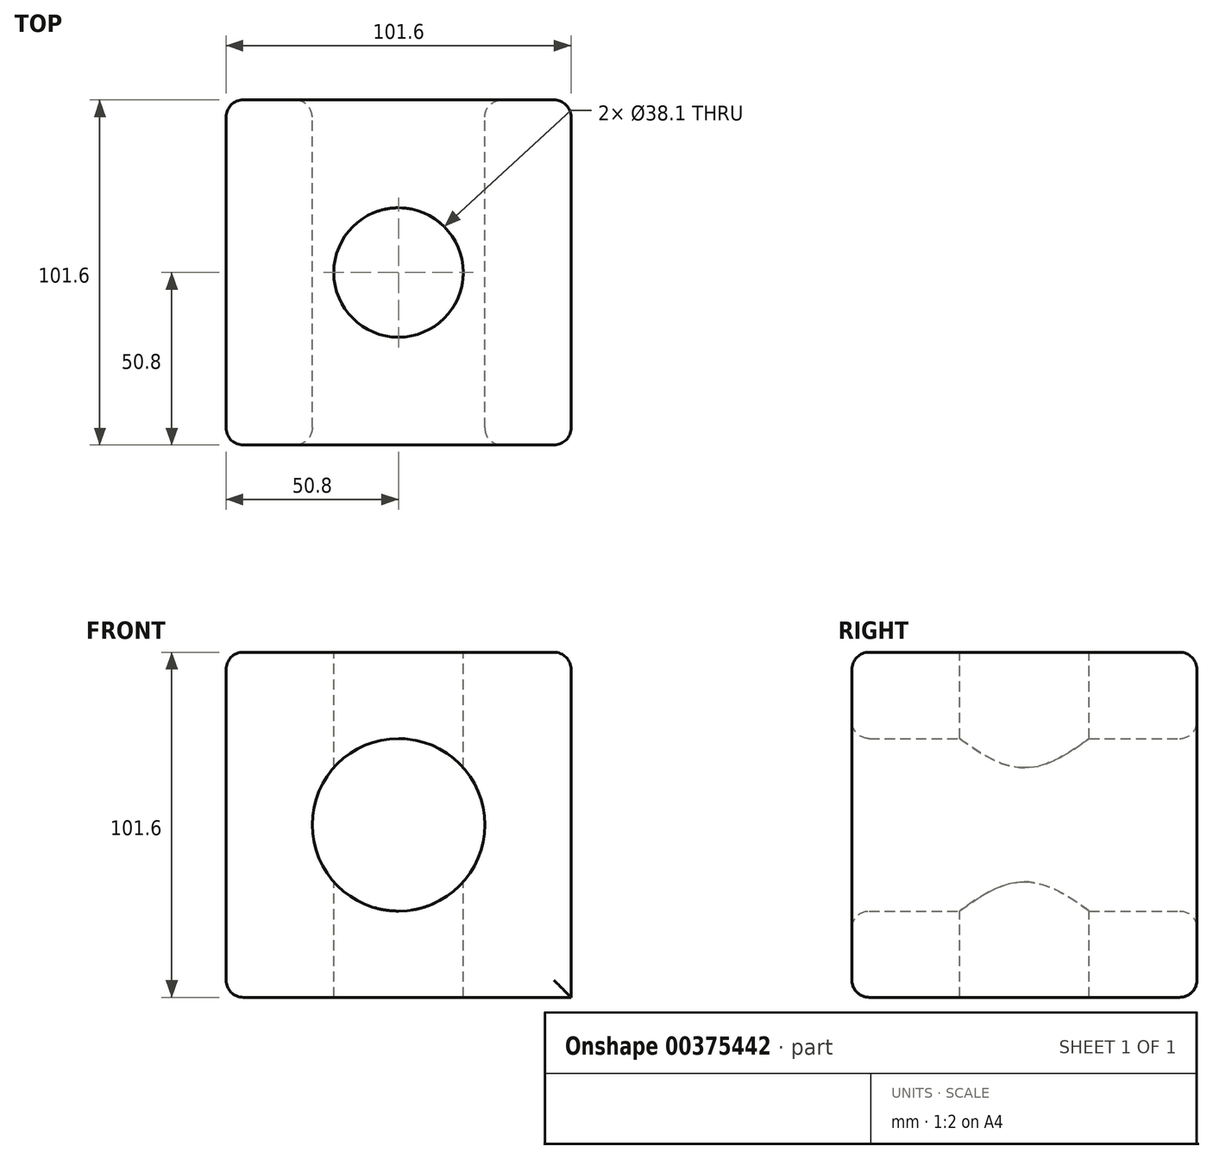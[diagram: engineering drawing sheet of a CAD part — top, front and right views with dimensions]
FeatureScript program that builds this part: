
annotation { "Feature Type Name" : "Feature", "Feature Type Description" : "" }
export const myFeature = defineFeature(function(context is Context, id is Id, definition is map)
    precondition{}
    {
        {
            var Q0;
            Q0=qCreatedBy(makeId("Front.planeOp"),FACE);
            var sketch = newSketch(context, id + "F0", { "sketchPlane" : qUnion([Q0])});
            skLineSegment(sketch, "E0.bottom", {"start": v(-50.8, 50.8) * mm, "end": v(50.8, 50.8) * mm});
            skLineSegment(sketch, "E0.top", {"start": v(-50.8, -50.8) * mm, "end": v(50.8, -50.8) * mm});
            skLineSegment(sketch, "E0.left", {"start": v(-50.8, 50.8) * mm, "end": v(-50.8, -50.8) * mm});
            skLineSegment(sketch, "E0.right", {"start": v(50.8, 50.8) * mm, "end": v(50.8, -50.8) * mm});
            skCircle(sketch, "E1", {"center": v(0, 0) * mm, "radius": 25.4 * mm});
            skSolve(sketch);
        }
        {
            var Q0;
            Q0=makeQuery(id+"F0.imprint","IMPRINT",FACE,{"disambiguationData":[TD([[makeQuery(id+"F0.imprint","IMPRINT",EDGE,{"derivedFrom":sQuery(id+"F0.wireOp",EDGE,"E0.bottom")}),-1.0]])]});
            extrude(context, id + "F1", {"entities" : qUnion([Q0]), "endBound" : BoundingType.SYMMETRIC, "depth" : 101.6 * mm});
        }
        {
            var Q0;
            Q0=makeQuery(id+"F1.opExtrude","CAP_EDGE",EDGE,{"disambiguationData":[OSD([sQuery(id+"F0.wireOp",EDGE,"E0.bottom")])],"isStart":false});
            var Q1;
            Q1=makeQuery(id+"F1.opExtrude","SWEPT_EDGE",EDGE,{"disambiguationData":[OSD([sQuery(id+"F0.wireOp",EDGE,"E0.bottom"),sQuery(id+"F0.wireOp",EDGE,"E0.left")])]});
            var Q2;
            Q2=makeQuery(id+"F1.opExtrude","SWEPT_FACE",FACE,{"disambiguationData":[OSD([sQuery(id+"F0.wireOp",EDGE,"E0.bottom")])]});
            var Q3;
            Q3=makeQuery(id+"F1.opExtrude","SWEPT_EDGE",EDGE,{"disambiguationData":[OSD([sQuery(id+"F0.wireOp",EDGE,"E0.bottom"),sQuery(id+"F0.wireOp",EDGE,"E0.right")])]});
            fillet(context, id + "F2", {"entities" : qUnion([Q0, Q1, Q2, Q3]), "radius" : 5.08 * mm, "tangentPropagation" : true, "allowEdgeOverflow" : false});
        }
        {
            var Q0;
            Q0=makeQuery(id+"F1.opExtrude","SWEPT_FACE",FACE,{"disambiguationData":[OSD([sQuery(id+"F0.wireOp",EDGE,"E0.left")])]});
            fillet(context, id + "F3", {"entities" : qUnion([Q0]), "radius" : 5.08 * mm, "tangentPropagation" : true, "allowEdgeOverflow" : false});
        }
        {
            var Q0;
            Q0=makeQuery(id+"F1.opExtrude","CAP_FACE",FACE,{"disambiguationData":[OSD([sQuery(id+"F0.wireOp",EDGE,"E0.bottom"),sQuery(id+"F0.wireOp",EDGE,"E0.top"),sQuery(id+"F0.wireOp",EDGE,"E0.left"),sQuery(id+"F0.wireOp",EDGE,"E0.right"),sQuery(id+"F0.wireOp",EDGE,"E1")])],"isStart":false});
            fillet(context, id + "F4", {"entities" : qUnion([Q0]), "radius" : 5.08 * mm, "tangentPropagation" : true, "allowEdgeOverflow" : false});
        }
        {
            var Q0;
            Q0=makeQuery(id+"F1.opExtrude","CAP_FACE",FACE,{"disambiguationData":[OSD([sQuery(id+"F0.wireOp",EDGE,"E0.bottom"),sQuery(id+"F0.wireOp",EDGE,"E0.top"),sQuery(id+"F0.wireOp",EDGE,"E0.left"),sQuery(id+"F0.wireOp",EDGE,"E0.right"),sQuery(id+"F0.wireOp",EDGE,"E1")])],"isStart":true});
            fillet(context, id + "F5", {"entities" : qUnion([Q0]), "radius" : 5.08 * mm, "tangentPropagation" : true, "allowEdgeOverflow" : false});
        }
        {
            var Q0;
            Q0=makeQuery(id+"F1.opExtrude","SWEPT_FACE",FACE,{"disambiguationData":[OSD([sQuery(id+"F0.wireOp",EDGE,"E0.bottom")])]});
            var sketch = newSketch(context, id + "F6", { "sketchPlane" : qUnion([Q0])});
            skCircle(sketch, "E2", {"center": v(0, 0) * mm, "radius": 19.05 * mm});
            skSolve(sketch);
        }
        {
            var Q0;
            Q0 = qSketchRegion(id + "F6", true);
            extrude(context, id + "F7", {"entities" : qUnion([Q0]), "operationType" : NewBodyOperationType.REMOVE, "endBound" : BoundingType.THROUGH_ALL, "oppositeDirection" : true, "depth" : 25.4 * mm});
        }
    });
